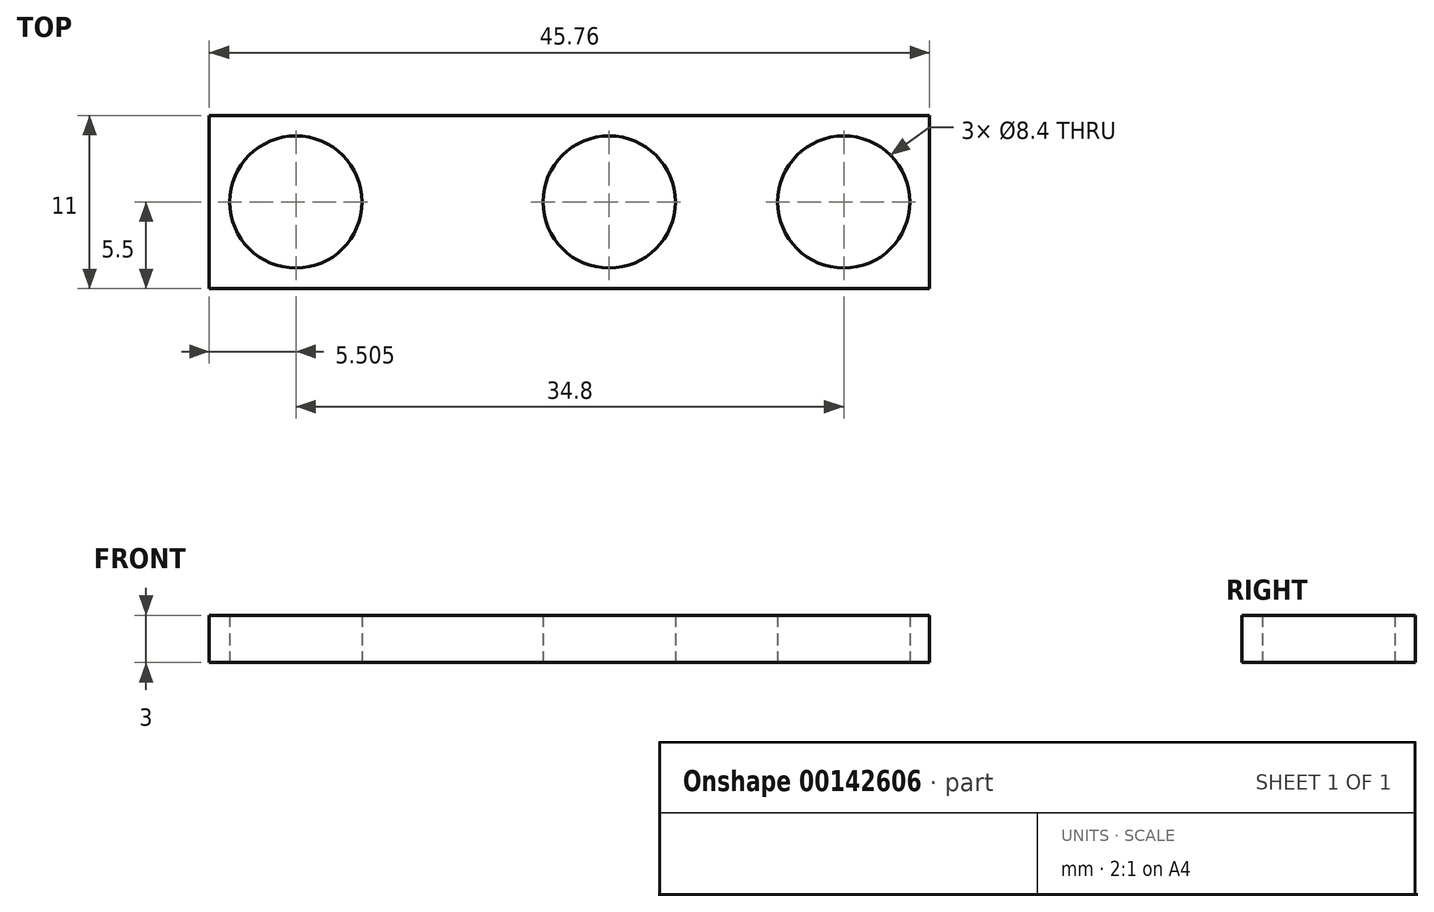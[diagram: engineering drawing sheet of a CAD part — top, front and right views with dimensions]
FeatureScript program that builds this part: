
annotation { "Feature Type Name" : "Feature", "Feature Type Description" : "" }
export const myFeature = defineFeature(function(context is Context, id is Id, definition is map)
    precondition{}
    {
        {
            var Q0;
            Q0=qCreatedBy(makeId("Top.planeOp"),FACE);
            var sketch = newSketch(context, id + "F0", { "sketchPlane" : qUnion([Q0])});
            skLineSegment(sketch, "E0.bottom", {"start": v(22.88, 5.5) * mm, "end": v(-22.88, 5.5) * mm});
            skLineSegment(sketch, "E0.top", {"start": v(22.88, -5.5) * mm, "end": v(-22.88, -5.5) * mm});
            skLineSegment(sketch, "E0.left", {"start": v(22.88, 5.5) * mm, "end": v(22.88, -5.5) * mm});
            skLineSegment(sketch, "E0.right", {"start": v(-22.88, 5.5) * mm, "end": v(-22.88, -5.5) * mm});
            skPoint(sketch, "E0.middle", {"position": v(0, 0) * mm});
            skLineSegment(sketch, "E1", {"start": v(-22.88, 0) * mm, "end": v(-17.37, 0) * mm});
            skPoint(sketch, "E1.endSnap0", {"position": v(-22.88, 0) * mm});
            skCircle(sketch, "E2", {"center": v(-17.37, 0) * mm, "radius": 4.2 * mm});
            skLineSegment(sketch, "E3", {"start": v(-17.37, 0) * mm, "end": v(2.53, 0) * mm});
            skCircle(sketch, "E4", {"center": v(2.53, 0) * mm, "radius": 4.2 * mm});
            skLineSegment(sketch, "E5", {"start": v(2.53, 0) * mm, "end": v(17.43, 0) * mm});
            skCircle(sketch, "E6", {"center": v(17.43, 0) * mm, "radius": 4.2 * mm});
            skSolve(sketch);
        }
        {
            var Q0;
            {var subQ1=sQuery(id+"F0.wireOp",EDGE,"E0.bottom");Q0=makeQuery(id+"F0.imprint","IMPRINT",FACE,{"disambiguationData":[TD([[makeQuery(id+"F0.imprint","IMPRINT",EDGE,{"derivedFrom":subQ1}),1.0]])]});}
            extrude(context, id + "F1", {"entities" : qUnion([Q0]), "depth" : 3 * mm});
        }
    });
